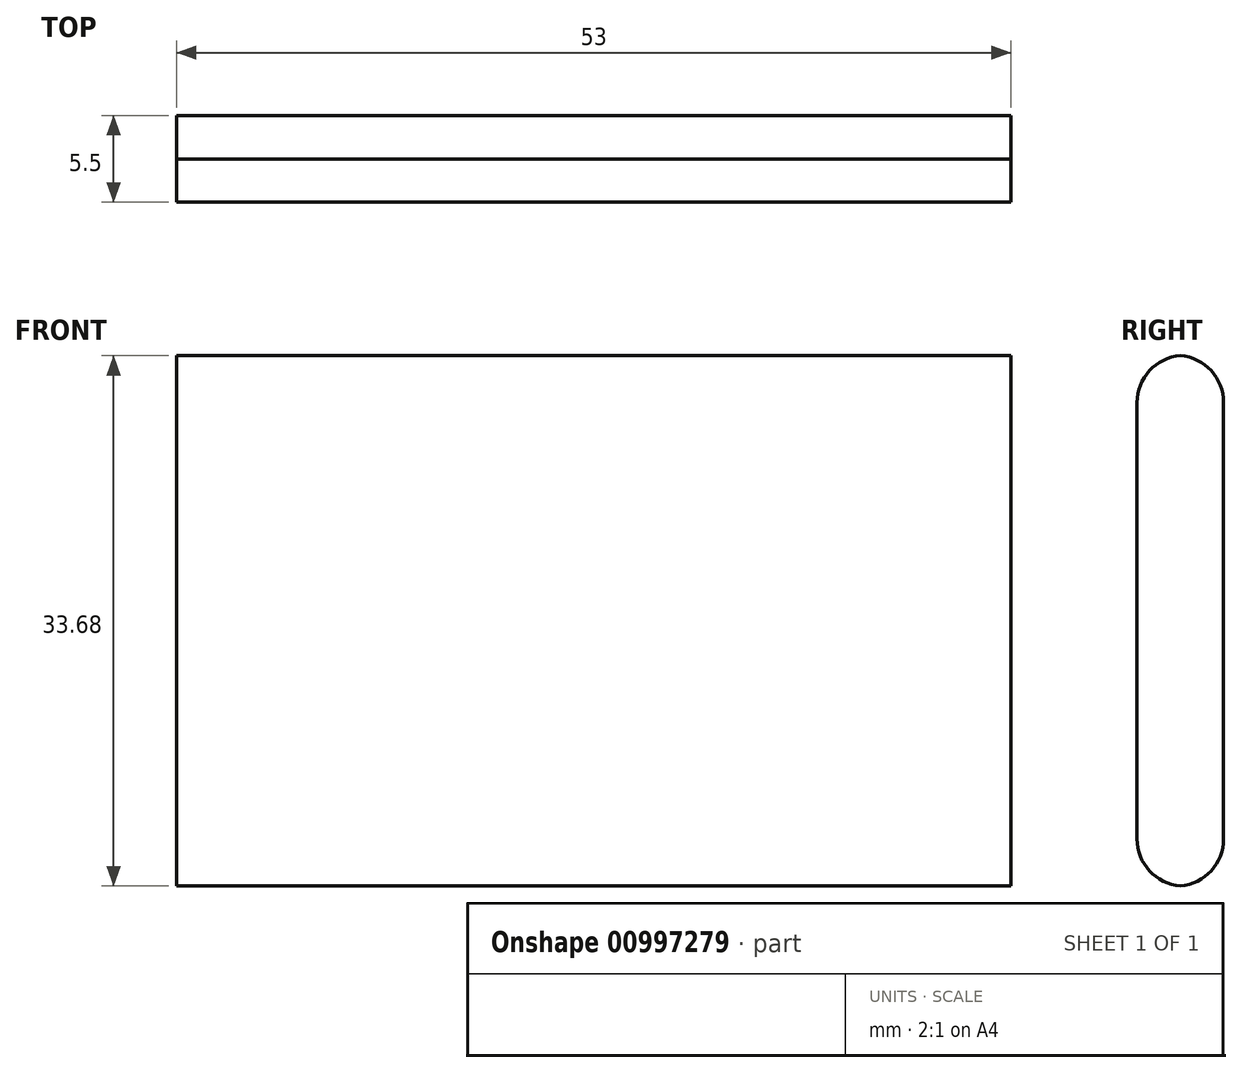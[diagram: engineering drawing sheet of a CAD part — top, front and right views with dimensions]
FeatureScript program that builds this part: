
annotation { "Feature Type Name" : "Feature", "Feature Type Description" : "" }
export const myFeature = defineFeature(function(context is Context, id is Id, definition is map)
    precondition{}
    {
        {
            var Q0;
            Q0=qCreatedBy(makeId("Front.planeOp"),FACE);
            var sketch = newSketch(context, id + "F0", { "sketchPlane" : qUnion([Q0])});
            skLineSegment(sketch, "E0.bottom", {"start": v(-50.63, 55.26) * mm, "end": v(2.37, 55.26) * mm});
            skLineSegment(sketch, "E0.top", {"start": v(-50.63, 21.56) * mm, "end": v(2.37, 21.56) * mm});
            skLineSegment(sketch, "E0.left", {"start": v(-50.63, 55.26) * mm, "end": v(-50.63, 21.56) * mm});
            skLineSegment(sketch, "E0.right", {"start": v(2.37, 55.26) * mm, "end": v(2.37, 21.56) * mm});
            skSolve(sketch);
        }
        {
            var Q0;
            Q0=makeQuery(id+"F0.imprint","IMPRINT",FACE,{"disambiguationData":[TD([[makeQuery(id+"F0.imprint","IMPRINT",EDGE,{"derivedFrom":sQuery(id+"F0.wireOp",EDGE,"E0.bottom")}),-1.0]])]});
            extrude(context, id + "F1", {"entities" : qUnion([Q0]), "depth" : 5.5 * mm, "offsetDistance" : 25 * mm});
        }
        {
            var Q0;
            Q0=makeQuery(id+"F1.opExtrude","CAP_EDGE",EDGE,{"disambiguationData":[OSD([sQuery(id+"F0.wireOp",EDGE,"E0.bottom")])],"isStart":false});
            var Q1;
            Q1=makeQuery(id+"F1.opExtrude","CAP_EDGE",EDGE,{"disambiguationData":[OSD([sQuery(id+"F0.wireOp",EDGE,"E0.bottom")])],"isStart":true});
            var Q2;
            Q2=makeQuery(id+"F1.opExtrude","CAP_EDGE",EDGE,{"disambiguationData":[OSD([sQuery(id+"F0.wireOp",EDGE,"E0.top")])],"isStart":true});
            var Q3;
            Q3=makeQuery(id+"F1.opExtrude","CAP_EDGE",EDGE,{"disambiguationData":[OSD([sQuery(id+"F0.wireOp",EDGE,"E0.top")])],"isStart":false});
            fillet(context, id + "F2", {"entities" : qUnion([Q0, Q1, Q2, Q3]), "radius" : 3 * mm, "tangentPropagation" : true, "allowEdgeOverflow" : false});
        }
    });
